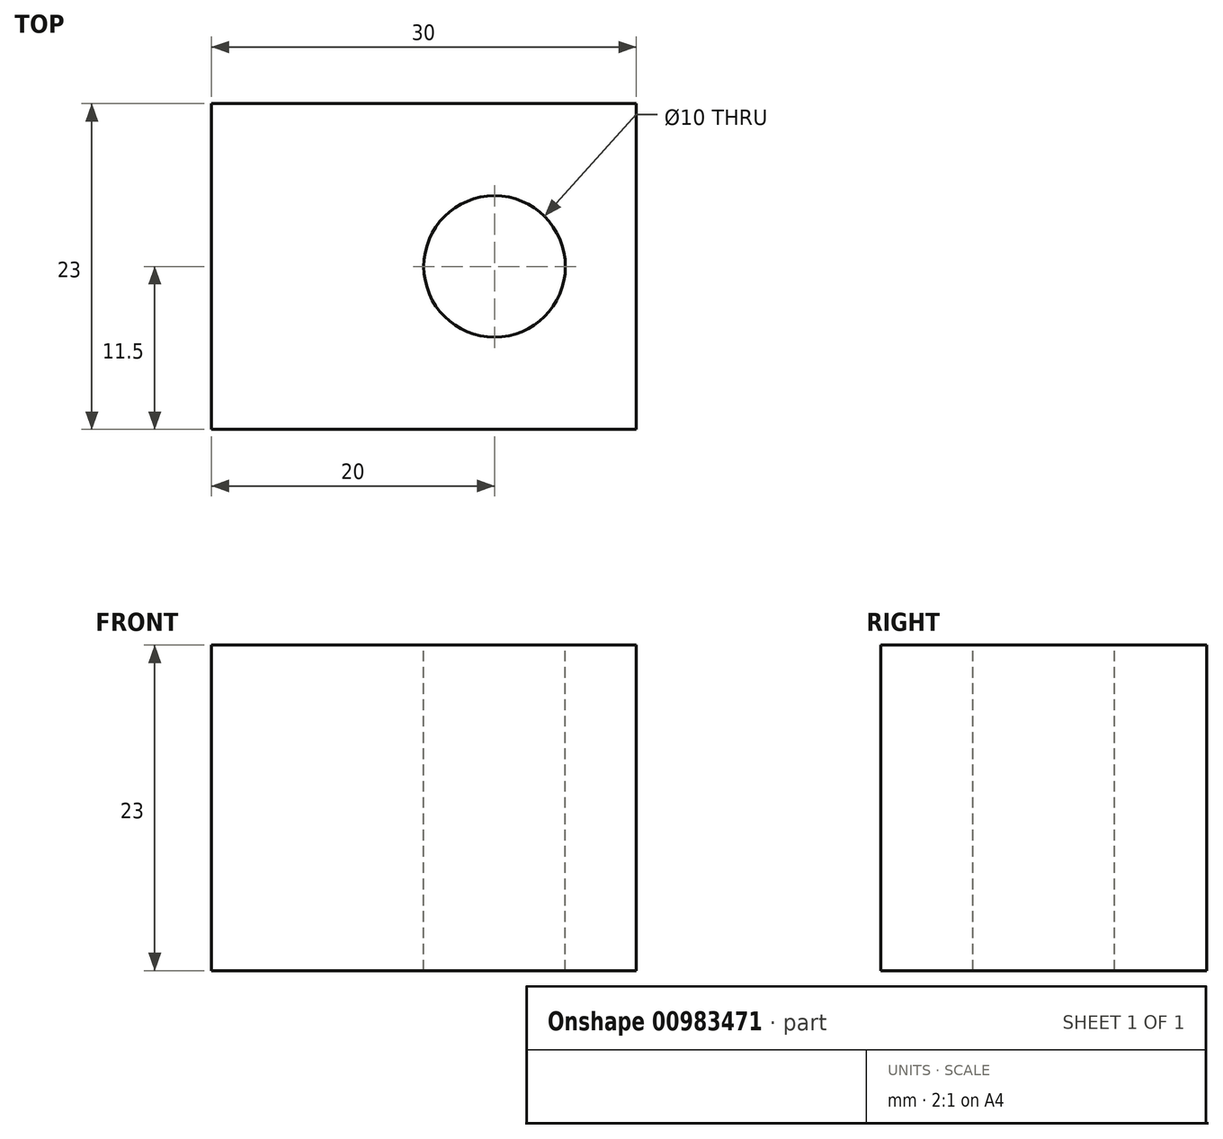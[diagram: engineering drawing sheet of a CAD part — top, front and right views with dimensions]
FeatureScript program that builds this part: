
annotation { "Feature Type Name" : "Feature", "Feature Type Description" : "" }
export const myFeature = defineFeature(function(context is Context, id is Id, definition is map)
    precondition{}
    {
        {
            var Q0;
            Q0=qCreatedBy(makeId("Right.planeOp"),FACE);
            var sketch = newSketch(context, id + "F0", { "sketchPlane" : qUnion([Q0])});
            skLineSegment(sketch, "E0.bottom", {"start": v(11.5, 11.5) * mm, "end": v(-11.5, 11.5) * mm});
            skLineSegment(sketch, "E0.top", {"start": v(11.5, -11.5) * mm, "end": v(-11.5, -11.5) * mm});
            skLineSegment(sketch, "E0.left", {"start": v(11.5, 11.5) * mm, "end": v(11.5, -11.5) * mm});
            skLineSegment(sketch, "E0.right", {"start": v(-11.5, 11.5) * mm, "end": v(-11.5, -11.5) * mm});
            skPoint(sketch, "E0.middle", {"position": v(0, 0) * mm});
            skSolve(sketch);
        }
        {
            var Q0;
            Q0=makeQuery(id+"F0.imprint","IMPRINT",FACE,{"disambiguationData":[TD([[makeQuery(id+"F0.imprint","IMPRINT",EDGE,{"derivedFrom":sQuery(id+"F0.wireOp",EDGE,"E0.bottom")}),1.0]])]});
            extrude(context, id + "F1", {"entities" : qUnion([Q0]), "depth" : 30 * mm, "offsetDistance" : 25 * mm});
        }
        {
            var Q0;
            Q0=makeQuery(id+"F1.opExtrude","SWEPT_FACE",FACE,{"disambiguationData":[OSD([sQuery(id+"F0.wireOp",EDGE,"E0.bottom")])]});
            var sketch = newSketch(context, id + "F2", { "sketchPlane" : qUnion([Q0])});
            skPoint(sketch, "E1", {"position": v(20, 0) * mm});
            skPoint(sketch, "E1.positionSnap0", {"position": v(30, 0) * mm});
            skSolve(sketch);
        }
        {
            var Q0;
            Q0=sQuery(id+"F2.wireOp",VERTEX,"E1");
            var Q1;
            Q1=makeQuery(id+"F1.opExtrude","SWEPT_BODY",BODY,{"disambiguationData":[OSD([sQuery(id+"F0.wireOp",EDGE,"E0.bottom"),sQuery(id+"F0.wireOp",EDGE,"E0.top"),sQuery(id+"F0.wireOp",EDGE,"E0.left"),sQuery(id+"F0.wireOp",EDGE,"E0.right")])]});
            hole(context, id + "F3", {"style" : HoleStyle.SIMPLE, "endStyle" : HoleEndStyle.THROUGH, "holeDiameter" : 10 * mm, "majorDiameter" : 5 * mm, "isTappedThrough" : true, "tappedDepth" : 12 * mm, "tapClearance" : 3, "locations" : qUnion([Q0]), "scope" : qUnion([Q1])});
        }
    });
